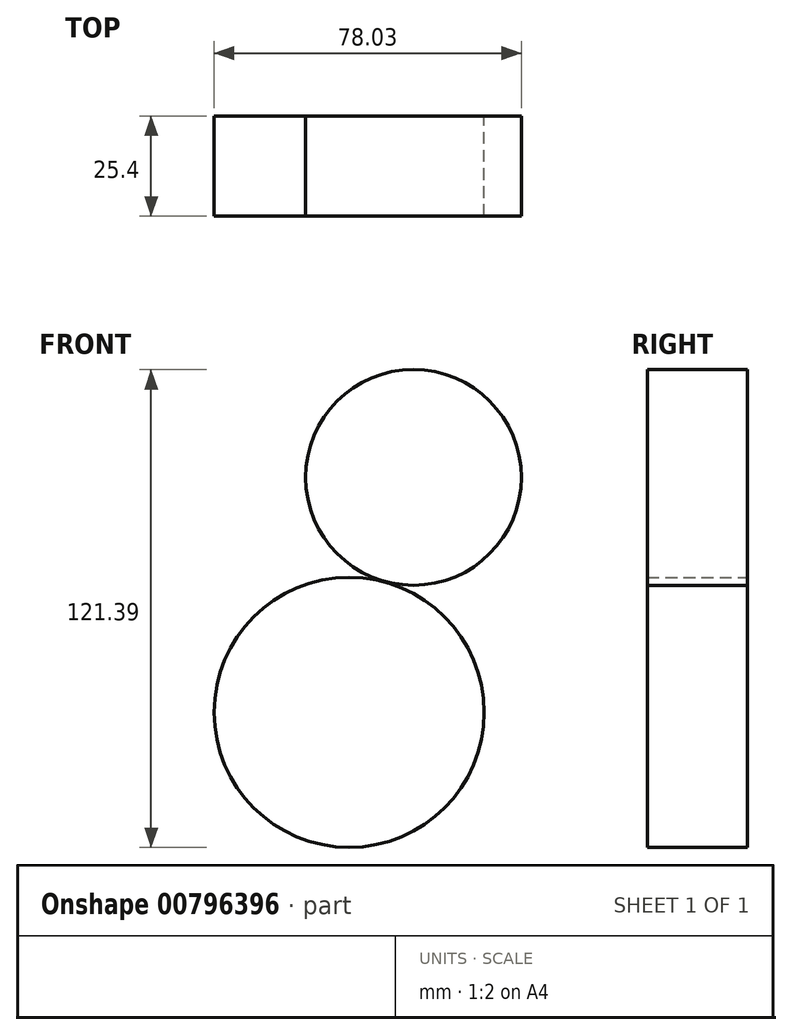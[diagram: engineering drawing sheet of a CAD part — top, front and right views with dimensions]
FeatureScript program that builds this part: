
annotation { "Feature Type Name" : "Feature", "Feature Type Description" : "" }
export const myFeature = defineFeature(function(context is Context, id is Id, definition is map)
    precondition{}
    {
        {
            var Q0;
            Q0=qCreatedBy(makeId("Front.planeOp"),FACE);
            var sketch = newSketch(context, id + "F0", { "sketchPlane" : qUnion([Q0])});
            skCircle(sketch, "E0", {"center": v(-15.24, 41.78) * mm, "radius": 27.4 * mm});
            skCircle(sketch, "E1", {"center": v(-31.57, -17.9) * mm, "radius": 34.3 * mm});
            skSolve(sketch);
        }
        {
            var Q0;
            Q0 = qSketchRegion(id + "F0", true);
            extrude(context, id + "F1", {"entities" : qUnion([Q0]), "depth" : 25.4 * mm, "offsetDistance" : 25.4 * mm});
        }
    });
